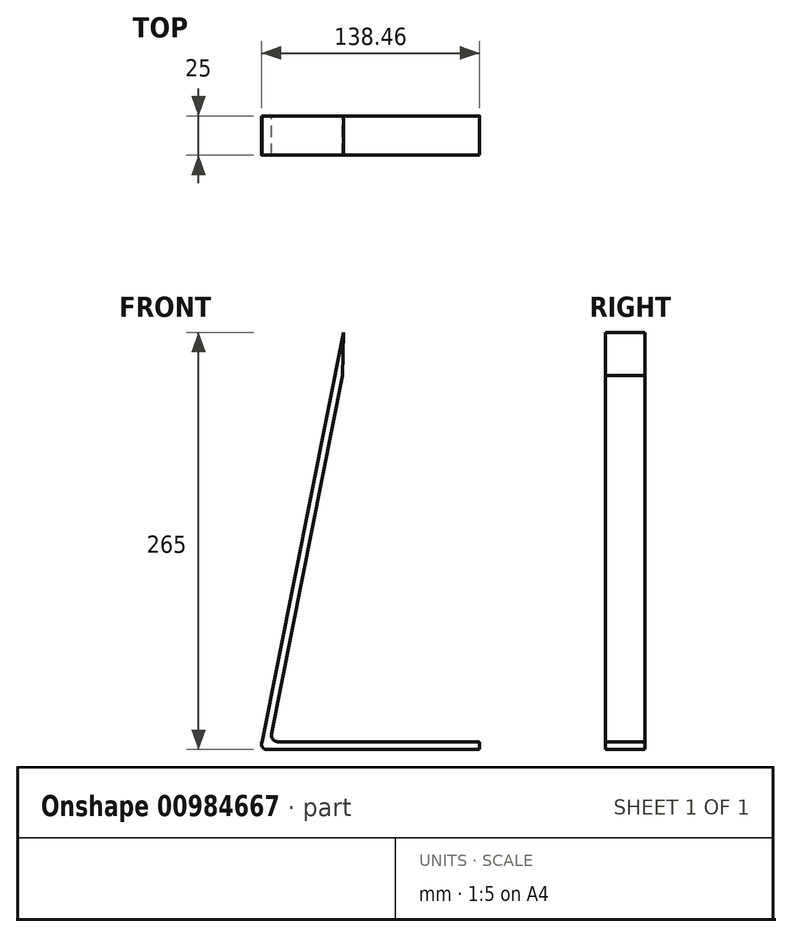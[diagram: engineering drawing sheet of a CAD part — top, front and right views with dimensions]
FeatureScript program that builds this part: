
annotation { "Feature Type Name" : "Feature", "Feature Type Description" : "" }
export const myFeature = defineFeature(function(context is Context, id is Id, definition is map)
    precondition{}
    {
        {
            var Q0;
            Q0=qCreatedBy(makeId("Front.planeOp"),FACE);
            var sketch = newSketch(context, id + "F0", { "sketchPlane" : qUnion([Q0])});
            skLineSegment(sketch, "E0", {"start": v(0, 0) * mm, "end": v(0, 5) * mm, "construction": true});
            skLineSegment(sketch, "E1", {"start": v(0, 5) * mm, "end": v(0, 75) * mm, "construction": true});
            skLineSegment(sketch, "E2", {"start": v(40, 0) * mm, "end": v(-95, 0) * mm});
            skArc(sketch, "E3", {"start": v(-98.23, 4.68) * mm, "mid": v(-97.84, 1.5) * mm, "end": v(-95, 0) * mm});
            skLineSegment(sketch, "E4.0", {"start": v(40, 5) * mm, "end": v(-87.77, 5) * mm});
            skLineSegment(sketch, "E5", {"start": v(40, 5) * mm, "end": v(40, 0) * mm});
            skLineSegment(sketch, "E6", {"start": v(0, 0) * mm, "end": v(-25.19, 0) * mm, "construction": true});
            skLineSegment(sketch, "E7", {"start": v(0, -1.41) * mm, "end": v(0, -9.84) * mm, "construction": true});
            skLineSegment(sketch, "E8", {"start": v(0, -9.84) * mm, "end": v(-50, -9.84) * mm, "construction": true});
            skLineSegment(sketch, "E9", {"start": v(-50, -9.84) * mm, "end": v(-49.81, 5) * mm, "construction": true});
            skLineSegment(sketch, "E10", {"start": v(-46.53, 265) * mm, "end": v(-98.23, 4.68) * mm});
            skLineSegment(sketch, "E11.0", {"start": v(-46.88, 237.6) * mm, "end": v(-92.1, 9.9) * mm});
            skLineSegment(sketch, "E12", {"start": v(-87.77, 5) * mm, "end": v(-88.07, 5) * mm});
            skArc(sketch, "E13", {"start": v(-92.1, 9.9) * mm, "mid": v(-91.25, 6.5) * mm, "end": v(-88.07, 5) * mm});
            skLineSegment(sketch, "E14", {"start": v(-46.53, 265) * mm, "end": v(-46.88, 237.6) * mm});
            skSolve(sketch);
        }
        {
            var Q0;
            Q0 = qSketchRegion(id + "F0", true);
            extrude(context, id + "F1", {"entities" : qUnion([Q0]), "depth" : 25 * mm, "offsetDistance" : 25 * mm});
        }
        {
            var Q0;
            Q0=makeQuery(id+"F1.opExtrude","SWEPT_EDGE",EDGE,{"disambiguationData":[OSD([sQuery(id+"F0.wireOp",EDGE,"E4.0"),sQuery(id+"F0.wireOp",EDGE,"E5")])]});
            var Q1;
            Q1=makeQuery(id+"F1.opExtrude","SWEPT_EDGE",EDGE,{"disambiguationData":[OSD([sQuery(id+"F0.wireOp",EDGE,"E2"),sQuery(id+"F0.wireOp",EDGE,"E5")])]});
            fillet(context, id + "F2", {"entities" : qUnion([Q0, Q1]), "radius" : 1 * mm, "tangentPropagation" : true, "allowEdgeOverflow" : false});
        }
    });
